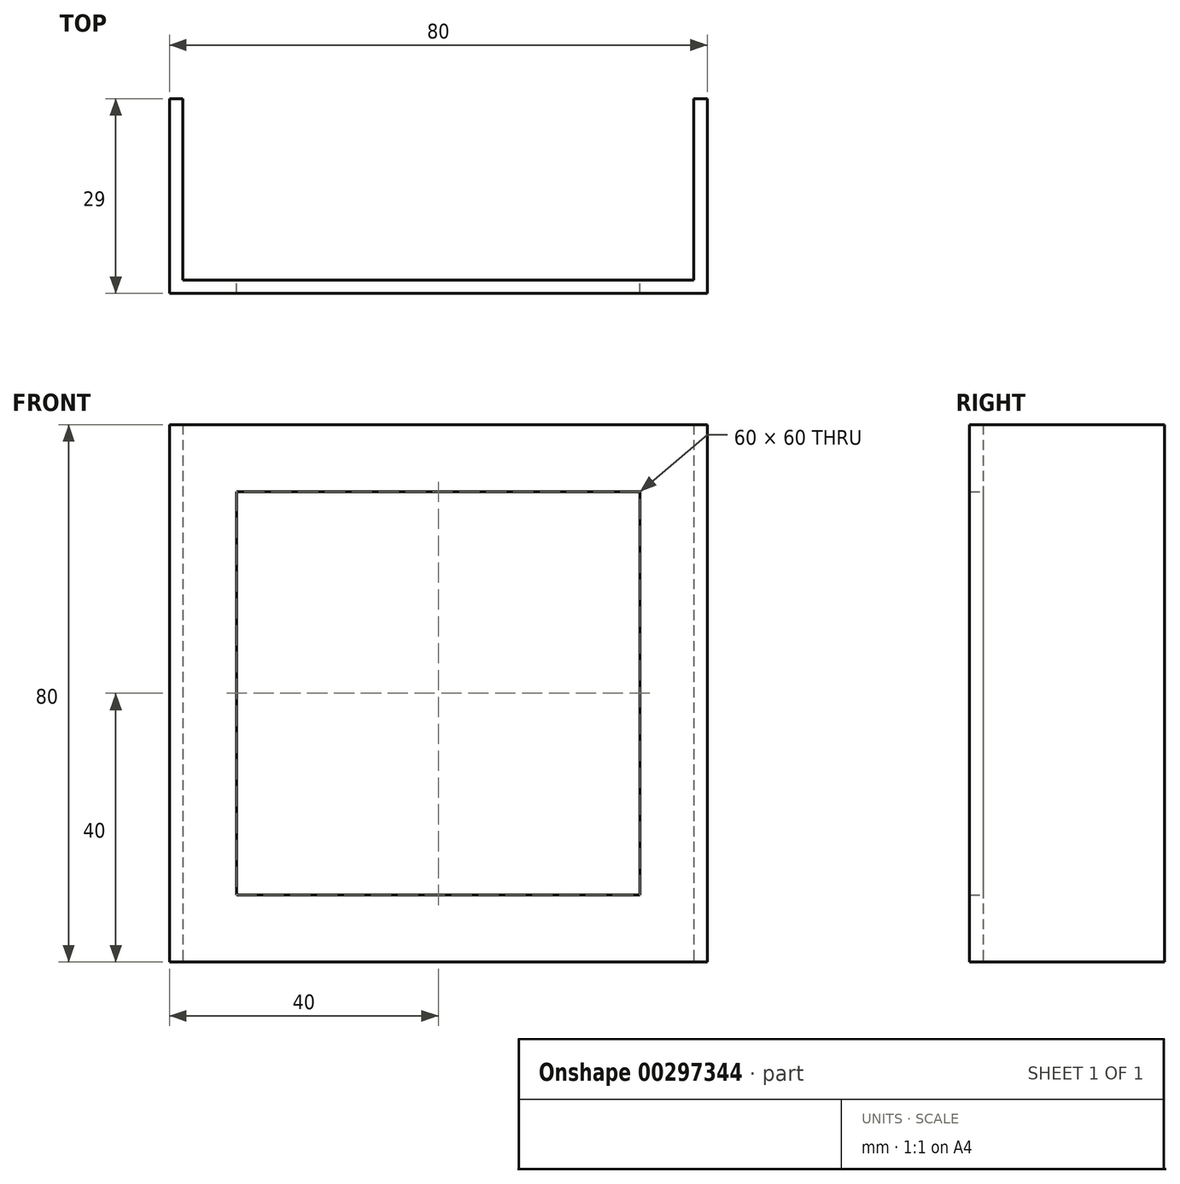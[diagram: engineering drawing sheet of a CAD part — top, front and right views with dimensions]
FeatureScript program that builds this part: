
annotation { "Feature Type Name" : "Feature", "Feature Type Description" : "" }
export const myFeature = defineFeature(function(context is Context, id is Id, definition is map)
    precondition{}
    {
        {
            var Q0;
            Q0=qCreatedBy(makeId("Front.planeOp"),FACE);
            var sketch = newSketch(context, id + "F0", { "sketchPlane" : qUnion([Q0])});
            skLineSegment(sketch, "E0.bottom", {"start": v(40, 40) * mm, "end": v(-40, 40) * mm});
            skLineSegment(sketch, "E0.top", {"start": v(40, -40) * mm, "end": v(-40, -40) * mm});
            skLineSegment(sketch, "E0.left", {"start": v(40, 40) * mm, "end": v(40, -40) * mm});
            skLineSegment(sketch, "E0.right", {"start": v(-40, 40) * mm, "end": v(-40, -40) * mm});
            skPoint(sketch, "E0.middle", {"position": v(0, 0) * mm});
            skLineSegment(sketch, "E1.bottom", {"start": v(30, 30) * mm, "end": v(-30, 30) * mm});
            skLineSegment(sketch, "E1.top", {"start": v(30, -30) * mm, "end": v(-30, -30) * mm});
            skLineSegment(sketch, "E1.left", {"start": v(30, 30) * mm, "end": v(30, -30) * mm});
            skLineSegment(sketch, "E1.right", {"start": v(-30, 30) * mm, "end": v(-30, -30) * mm});
            skSolve(sketch);
        }
        {
            var Q0;
            Q0=qSketchRegion(id+"F0",true);
            extrude(context, id + "F1", {"entities" : qUnion([Q0]), "depth" : 2 * mm});
        }
        {
            var Q0;
            Q0=makeQuery(id+"F1.opExtrude","CAP_FACE",FACE,{"disambiguationData":[OSD([sQuery(id+"F0.wireOp",EDGE,"E0.bottom"),sQuery(id+"F0.wireOp",EDGE,"E0.top"),sQuery(id+"F0.wireOp",EDGE,"E0.left"),sQuery(id+"F0.wireOp",EDGE,"E0.right"),sQuery(id+"F0.wireOp",EDGE,"E1.bottom"),sQuery(id+"F0.wireOp",EDGE,"E1.top"),sQuery(id+"F0.wireOp",EDGE,"E1.left"),sQuery(id+"F0.wireOp",EDGE,"E1.right")])],"isStart":true});
            var sketch = newSketch(context, id + "F2", { "sketchPlane" : qUnion([Q0])});
            skLineSegment(sketch, "E2.bottom", {"start": v(-40, 40) * mm, "end": v(-38, 40) * mm});
            skLineSegment(sketch, "E2.top", {"start": v(-40, -40) * mm, "end": v(-38, -40) * mm});
            skLineSegment(sketch, "E2.left", {"start": v(-40, 40) * mm, "end": v(-40, -40) * mm});
            skLineSegment(sketch, "E2.right", {"start": v(-38, 40) * mm, "end": v(-38, -40) * mm});
            skLineSegment(sketch, "E3.bottom", {"start": v(40, 40) * mm, "end": v(38, 40) * mm});
            skLineSegment(sketch, "E3.top", {"start": v(40, -40) * mm, "end": v(38, -40) * mm});
            skLineSegment(sketch, "E3.left", {"start": v(40, 40) * mm, "end": v(40, -40) * mm});
            skLineSegment(sketch, "E3.right", {"start": v(38, 40) * mm, "end": v(38, -40) * mm});
            skSolve(sketch);
        }
        {
            var Q0;
            Q0=qSketchRegion(id+"F2",true);
            extrude(context, id + "F3", {"entities" : qUnion([Q0]), "operationType" : NewBodyOperationType.ADD, "depth" : 27 * mm});
        }
    });
